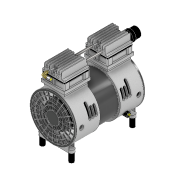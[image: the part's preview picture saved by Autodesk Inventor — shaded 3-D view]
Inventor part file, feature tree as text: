
AUTODESK INVENTOR PART (.ipt)
format: ipt  version: 2022 (Build 260153000, 153)  size: 2,104,832 bytes
history: native  units: mm
features: sketch x43, extrude x40, projected_geometry x15, fillet x4, plane x2, thread x2, boolean_combine x1, sweep x1
ambient origin geometry x8: Origin, YZ Plane, XZ Plane, XY Plane, X Axis, Y Axis, Z Axis, Center Point
bodies: Solid1 (feature_tree), Solid2 (feature_tree), Solid3 (feature_tree), Solid4 (feature_tree), Solid5 (feature_tree), Solid6 (feature_tree), Solid7 (feature_tree), Solid8 (feature_tree), Solid9 (feature_tree), Solid10 (feature_tree), Solid12 (feature_tree), Solid13 (feature_tree), Solid14 (feature_tree), Solid15 (feature_tree), Solid16 (feature_tree), Solid17 (feature_tree), Solid19 (feature_tree)
feature tree (108):
  extrude  "Extrusion1"  Depth=15.0mm
  extrude  "Extrusion2"  Depth=15.0mm
  extrude  "Extrusion3"  Depth=19.0mm
  extrude  "Extrusion4"  Depth=10.0mm TaperAngle=0.0deg
  boolean_combine  "Combine1"
  extrude  "Extrusion5"  Depth=10.0mm TaperAngle=0.0deg
  extrude  "Extrusion6"  Depth=80.0mm TaperAngle=0.0deg
  extrude  "Extrusion7"  Depth=10.0mm TaperAngle=0.0deg
  extrude  "Extrusion8"  Depth=10.0mm TaperAngle=0.0deg
  extrude  "Extrusion9"  Depth=10.0mm TaperAngle=0.0deg
  extrude  "Extrusion10"  Depth=10.0mm TaperAngle=0.0deg
  extrude  "Extrusion11"  Depth=35.0mm
  extrude  "Extrusion12"  Depth=0.087266mm
  extrude  "Extrusion13"  Depth=2.530727mm
  extrude  "Extrusion14"  Depth=5.0mm TaperAngle=0.0deg
  extrude  "Extrusion15"  Depth=5.0mm TaperAngle=0.0deg
  extrude  "Extrusion16"  Depth=25.0mm
  plane  "Work Plane1"
  extrude  "Extrusion17"  Depth=8.0mm
  extrude  "Extrusion18"  Depth=8.0mm
  extrude  "Extrusion19"  Depth=11.0mm
  sketch  "Sketch21"  dims[d60=11.0mm d61=0.0mm d62=0.0mm]
  plane  "Work Plane2"
  extrude  "Extrusion20"  TaperAngle=0.0deg  [1 undecoded]
  extrude  "Extrusion21"  Depth=10.0mm TaperAngle=0.0deg
  extrude  "Extrusion22"  Depth=5.0mm
  extrude  "Extrusion23"  Depth=5.0mm TaperAngle=0.0deg
  extrude  "Extrusion24"  Depth=10.0mm
  extrude  "Extrusion25"  Depth=80.0mm
  extrude  "Extrusion26"  Depth=5.0mm
  extrude  "Extrusion27"  Depth=10.0mm
  extrude  "Extrusion28"  Depth=8.0mm
  extrude  "Extrusion29"  Depth=8.0mm
  fillet  "Fillet1"  Radius=4.0mm
  fillet  "Fillet2"  Radius=8.0mm
  fillet  "Fillet3"  Radius=4.0mm
  fillet  "Fillet4"  Radius=4.0mm
  extrude  "Extrusion30"  Depth=5.0mm TaperAngle=0.0deg
  extrude  "Extrusion31"  Depth=5.0mm TaperAngle=0.0deg
  extrude  "Extrusion32"  Depth=55.0mm
  extrude  "Extrusion33"  Depth=5.0mm
  extrude  "Extrusion34"  Depth=10.0mm
  extrude  "Extrusion35"  Depth=5.0mm TaperAngle=0.0deg
  extrude  "Extrusion36"  Depth=6.28mm
  extrude  "Extrusion37"  Depth=6.28mm
  extrude  "Extrusion38"  Depth=2.0mm
  sweep  "Sweep1"
  extrude  "Extrusion39"  Depth=2.0mm
  thread  "Thread1"  [1 undecoded]
  thread  "Thread2"  [1 undecoded]
  extrude  "Extrusion40"  Depth=4.0mm
  sketch  "Sketch1"  dims[d0=15.0mm d1=15.0mm]
  sketch  "Sketch2"  dims[d2=15.0mm d3=15.0mm]
  projected_geometry  "Projected Loop1"
  projected_geometry  "Projected Loop2"
  sketch  "Sketch3"  dims[d4=30.0mm d5=0.0mm d6=19.0mm]
  sketch  "Sketch4"  dims[d7=19.0mm d8=10.0mm d9=0.0mm]
  projected_geometry  "Projected Loop3"
  sketch  "Sketch5"  dims[d10=10.0mm d11=0.0mm d12=10.0mm d13=0.0mm]
  sketch  "Sketch6"  dims[d14=80.0mm d15=0.0mm d16=80.0mm d17=0.0mm]
  sketch  "Sketch7"  dims[d18=10.0mm d19=0.0mm d20=10.0mm d21=0.0mm]
  sketch  "Sketch8"  dims[d22=88.0mm d23=10.0mm d24=0.0mm]
  sketch  "Sketch9"  dims[d25=88.0mm d26=10.0mm d27=0.0mm]
  sketch  "Sketch10"  dims[d28=10.0mm d29=0.0mm d30=10.0mm d31=0.0mm]
  sketch  "Sketch11"  dims[d32=30.0deg d33=35.0mm]
  projected_geometry  "Projected Loop4"
  sketch  "Sketch12"  dims[d34=0.087266mm d35=0.087266mm]
  projected_geometry  "Projected Loop5"
  sketch  "Sketch13"  dims[d36=2.530727mm d37=2.530727mm]
  sketch  "Sketch14"  dims[d38=120.0mm d40=360.0deg d42=5.0mm d43=0.0mm]
  projected_geometry  "Projected Loop6"
  sketch  "Sketch15"  dims[d44=5.0mm d45=0.0mm d46=5.0mm d47=0.0mm]
  sketch  "Sketch16"  dims[d48=11.786mm d49=0.0mm d50=25.0mm]
  sketch  "Sketch18"  dims[d51=0.0mm d52=8.0mm]
  sketch  "Sketch19"  dims[d53=25.0mm d54=0.0mm d55=8.0mm d56=8.0mm]
  sketch  "Sketch20"  dims[d57=11.0mm d59=11.0mm]
  projected_geometry  "Projected Loop7"
  sketch  "Sketch22"  dims[d63=15.0mm d64=10.0mm d65=0.0mm]
  sketch  "Sketch24"  dims[d66=5.0mm d67=0.0mm d68=35.0mm]
  projected_geometry  "Projected Loop12"
  projected_geometry  "Projected Loop13"
  sketch  "Sketch25"  dims[d69=70.0mm d70=5.0mm d71=0.0mm]
  sketch  "Sketch26"  dims[d72=10.0mm d73=0.0mm d74=40.0mm]
  sketch  "Sketch27"  dims[d75=5.0mm d76=80.0mm]
  sketch  "Sketch28"  dims[d77=40.0mm d78=5.0mm]
  projected_geometry  "Projected Loop14"
  sketch  "Sketch29"  dims[d79=10.0mm d80=0.0mm d81=12.0mm]
  sketch  "Sketch30"  dims[d82=8.0mm d83=12.0mm]
  projected_geometry  "Projected Loop15"
  sketch  "Sketch31"  dims[d84=8.0mm d85=8.0mm d86=4.0mm d87=8.0mm d88=4.0mm d89=4.0mm]
  projected_geometry  "Projected Loop16"
  projected_geometry  "Projected Loop17"
  sketch  "Sketch32"  dims[d90=15.0mm d91=0.0mm d92=5.0mm d93=0.0mm]
  projected_geometry  "Projected Loop18"
  sketch  "Sketch33"  dims[d94=4.0mm d95=5.0mm d96=0.0mm]
  sketch  "Sketch34"  dims[d97=55.0mm d98=55.0mm]
  sketch  "Sketch35"  dims[d99=5.0mm d100=0.0mm d101=60.0mm]
  sketch  "Sketch36"  dims[d102=5.0mm d103=10.0mm]
  sketch  "Sketch37"  dims[d104=15.0mm d105=0.0mm d106=5.0mm d107=0.0mm]
  sketch  "Sketch38"  dims[d108=2.0mm d109=6.28mm]
  sketch  "Sketch39"  dims[d110=2.0mm d111=6.28mm]
  sketch  "Sketch40"  dims[d112=2.0mm d113=2.0mm]
  sketch  "Sketch41"  dims[d114=6.28mm d115=2.0mm]
  sketch  "Sketch42"  dims[d116=6.28mm d117=2.0mm d118=2.0mm d119=2.0mm]
  sketch  "3D Sketch1"
  sketch  "Sketch43"  dims[d121=13.0mm d122=0.0mm d123=4.0mm]
  projected_geometry  "Projected Loop19"
  sketch  "Sketch44"  dims[d124=4.0mm d125=4.0mm d126=4.0mm d127=8.0mm d128=13.0mm d129=0.0mm d130=10.0mm d131=0.0mm d132=10.0mm d133=0.0mm d134=2.0mm d135=0.0mm d136=2.0mm d137=0.0mm d138=10.0mm d139=0.0mm d140=33.0mm d141=20.0mm d142=0.0mm d143=8.0mm d144=6.0mm d145=8.0mm d146=0.0mm d147=5.0mm d148=0.0mm d149=15.0mm d150=15.0mm d151=5.0mm d152=0.0mm d153=0.0mm d154=3.0mm d155=0.0mm d156=3.0mm d157=0.0mm d158=5.0mm d159=0.0mm d160=10.0mm d161=0.0mm]
note: 3 required parameter values undecoded (feature->parameter linkage not recoverable at this tier; creation-order binding heuristic only, values carry confidence <= 0.55)
